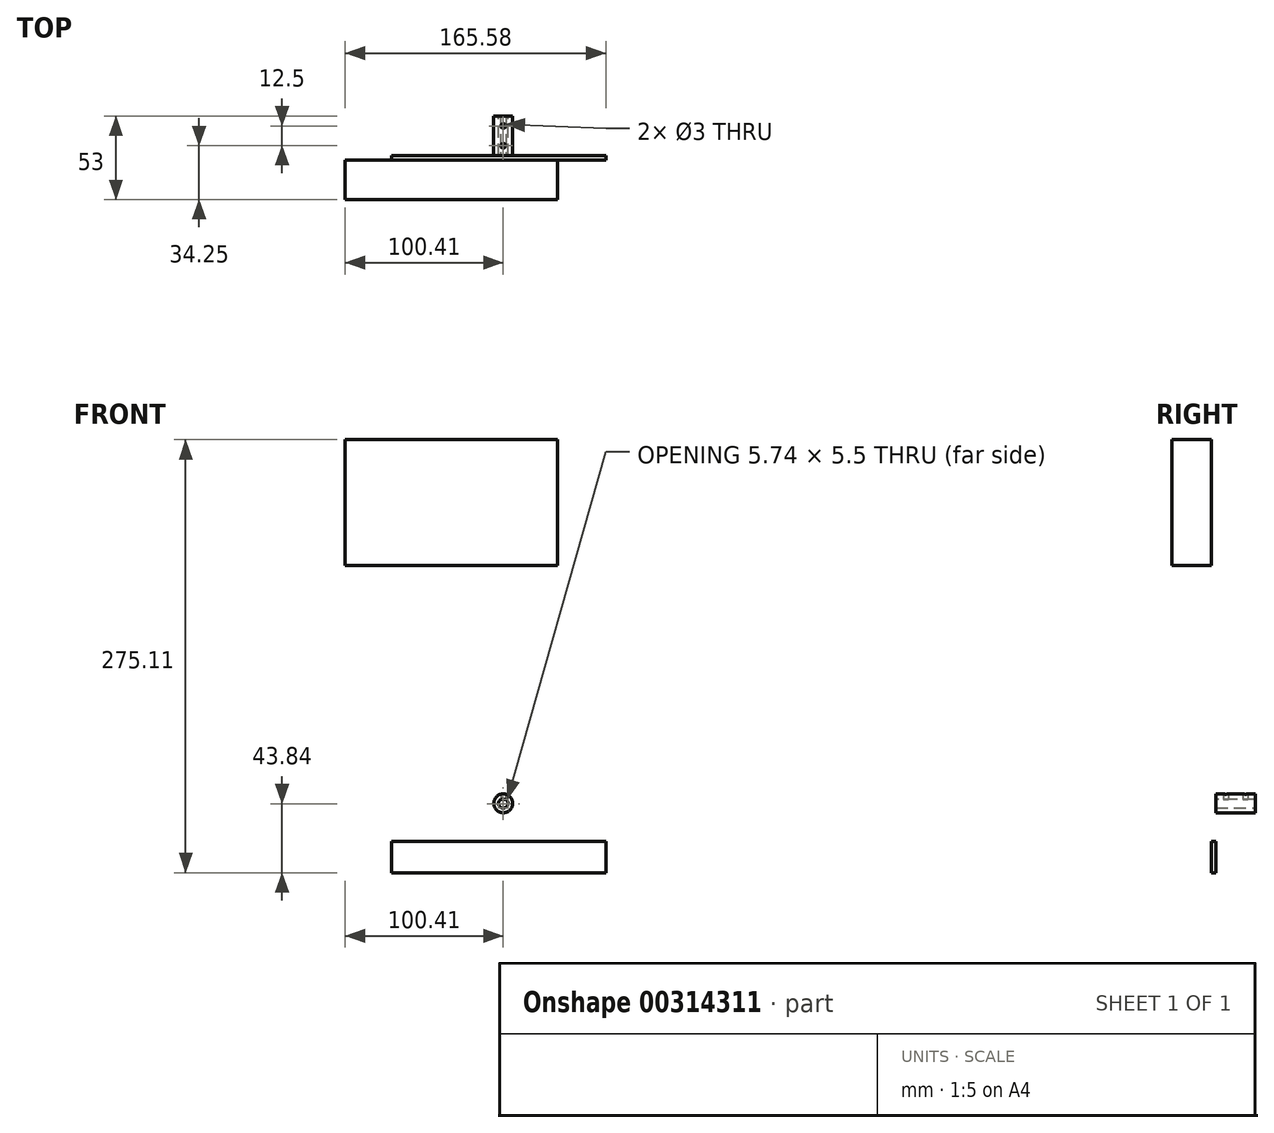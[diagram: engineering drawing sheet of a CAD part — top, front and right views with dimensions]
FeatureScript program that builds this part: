
annotation { "Feature Type Name" : "Feature", "Feature Type Description" : "" }
export const myFeature = defineFeature(function(context is Context, id is Id, definition is map)
    precondition{}
    {
        {
            var Q0;
            Q0=qCreatedBy(makeId("Front.planeOp"),FACE);
            var sketch = newSketch(context, id + "F0", { "sketchPlane" : qUnion([Q0])});
            skCircle(sketch, "E0", {"center": v(0, 0) * mm, "radius": 6 * mm});
            skSolve(sketch);
        }
        {
            var Q0;
            Q0=makeQuery(id+"F0.imprint","IMPRINT",FACE,{"disambiguationData":[TD([[makeQuery(id+"F0.imprint","IMPRINT",EDGE,{"derivedFrom":sQuery(id+"F0.wireOp",EDGE,"E0")}),1.0]])]});
            extrude(context, id + "F1", {"entities" : qUnion([Q0]), "depth" : 25 * mm});
        }
        {
            var Q0;
            Q0=qCreatedBy(makeId("Front.planeOp"),FACE);
            var sketch = newSketch(context, id + "F2", { "sketchPlane" : qUnion([Q0])});
            skCircle(sketch, "E1", {"center": v(0, 0) * mm, "radius": 3 * mm});
            skSolve(sketch);
        }
        {
            var Q0;
            Q0=makeQuery(id+"F2.imprint","IMPRINT",FACE,{"disambiguationData":[TD([[makeQuery(id+"F2.imprint","IMPRINT",EDGE,{"derivedFrom":sQuery(id+"F2.wireOp",EDGE,"E1")}),1.0]])]});
            var Q1;
            Q1=sQuery(id+"F2.wireOp",EDGE,"E1");
            var Q2;
            Q2=makeQuery(id+"F1.opExtrude","CAP_FACE",FACE,{"disambiguationData":[OSD([sQuery(id+"F0.wireOp",EDGE,"E0")])],"isStart":false});
            extrude(context, id + "F3", {"entities" : qUnion([Q0]), "operationType" : NewBodyOperationType.REMOVE, "surfaceEntities" : qUnion([Q1]), "endBound" : BoundingType.UP_TO_SURFACE, "endBoundEntityFace" : qUnion([Q2]), "depth" : 25 * mm});
        }
        {
            var Q0;
            Q0=makeQuery(id+"F1.opExtrude","CAP_FACE",FACE,{"disambiguationData":[OSD([sQuery(id+"F0.wireOp",EDGE,"E0")])],"isStart":false});
            var sketch = newSketch(context, id + "F4", { "sketchPlane" : qUnion([Q0])});
            skLineSegment(sketch, "E2", {"start": v(0, 2.5) * mm, "end": v(-1.66, 2.5) * mm});
            skLineSegment(sketch, "E3", {"start": v(-1.66, 2.5) * mm, "end": v(1.66, 2.5) * mm});
            skSolve(sketch);
        }
        {
            var Q0;
            Q0 = qSketchRegion(id + "F4", true);
            var Q1;
            {var subQ0=sQuery(id+"F4.wireOp",EDGE,"E3");var subQ3=makeQuery(id+"F4.imprint","IMPRINT",VERTEX,{"derivedFrom":subQ0});Q1=makeQuery(id+"F4.imprint","IMPRINT",FACE,{"disambiguationData":[TD([[makeQuery(id+"F4.imprint","IMPRINT",EDGE,{"disambiguationData":[TD([[subQ3,1.0]])],"derivedFrom":subQ0}),1.0]])]});}
            var Q2;
            Q2=makeQuery(id+"F1.opExtrude","CAP_FACE",FACE,{"disambiguationData":[OSD([sQuery(id+"F0.wireOp",EDGE,"E0")])],"isStart":true});
            extrude(context, id + "F5", {"entities" : qUnion([Q0, Q1]), "operationType" : NewBodyOperationType.ADD, "endBound" : BoundingType.UP_TO_SURFACE, "oppositeDirection" : true, "endBoundEntityFace" : qUnion([Q2]), "depth" : 25 * mm});
        }
        {
            var Q0;
            Q0=makeQuery(id+"F5.opExtrude","SWEPT_FACE",FACE,{"disambiguationData":[OSD([sQuery(id+"F4.wireOp",EDGE,"E3")])]});
            var sketch = newSketch(context, id + "F6", { "sketchPlane" : qUnion([Q0])});
            skLineSegment(sketch, "E4", {"start": v(-1.66, 12.5) * mm, "end": v(1.66, 12.5) * mm, "construction": true});
            skLineSegment(sketch, "E5", {"start": v(0, 12.5) * mm, "end": v(0, 25) * mm, "construction": true});
            skLineSegment(sketch, "E6", {"start": v(0, 12.5) * mm, "end": v(0, 0) * mm, "construction": true});
            skCircle(sketch, "E7", {"center": v(0, 18.75) * mm, "radius": 1.5 * mm});
            skCircle(sketch, "E8", {"center": v(0, 6.25) * mm, "radius": 1.5 * mm});
            skSolve(sketch);
        }
        {
            var Q0;
            Q0=makeQuery(id+"F6.imprint","IMPRINT",FACE,{"disambiguationData":[TD([[makeQuery(id+"F6.imprint","IMPRINT",EDGE,{"derivedFrom":sQuery(id+"F6.wireOp",EDGE,"E7")}),1.0]])]});
            var Q1;
            Q1=makeQuery(id+"F6.imprint","IMPRINT",FACE,{"disambiguationData":[TD([[makeQuery(id+"F6.imprint","IMPRINT",EDGE,{"derivedFrom":sQuery(id+"F6.wireOp",EDGE,"E8")}),1.0]])]});
            extrude(context, id + "F7", {"entities" : qUnion([Q0, Q1]), "operationType" : NewBodyOperationType.REMOVE, "endBound" : BoundingType.UP_TO_NEXT, "oppositeDirection" : true, "depth" : 25 * mm});
        }
        {
            var Q0;
            {var subQ0=sQuery(id+"F0.wireOp",EDGE,"E0");Q0=makeQuery(id+"F5.boolean.opBoolean","MERGE",FACE,{"derivedFrom":[makeQuery(id+"F1.opExtrude","CAP_FACE",FACE,{"disambiguationData":[OSD([subQ0])],"isStart":false}),makeQuery(id+"F5.opExtrude","CAP_FACE",FACE,{"disambiguationData":[OSD([subQ0,sQuery(id+"F2.wireOp",EDGE,"E1"),sQuery(id+"F4.wireOp",EDGE,"E3")])],"isStart":true})]});}
            var sketch = newSketch(context, id + "F8", { "sketchPlane" : qUnion([Q0])});
            skLineSegment(sketch, "E9.bottom", {"start": v(-70.83, -24.09) * mm, "end": v(65.17, -24.09) * mm});
            skLineSegment(sketch, "E9.top", {"start": v(-70.83, -44.09) * mm, "end": v(65.17, -44.09) * mm});
            skLineSegment(sketch, "E9.left", {"start": v(-70.83, -24.09) * mm, "end": v(-70.83, -44.09) * mm});
            skLineSegment(sketch, "E9.right", {"start": v(65.17, -24.09) * mm, "end": v(65.17, -44.09) * mm});
            skSolve(sketch);
        }
        {
            var Q0;
            Q0 = qSketchRegion(id + "F8", true);
            extrude(context, id + "F9", {"entities" : qUnion([Q0]), "depth" : 3 * mm});
        }
        {
            var Q0;
            {var subQ0=sQuery(id+"F0.wireOp",EDGE,"E0");Q0=makeQuery(id+"F5.boolean.opBoolean","MERGE",FACE,{"derivedFrom":[makeQuery(id+"F1.opExtrude","CAP_FACE",FACE,{"disambiguationData":[OSD([subQ0])],"isStart":false}),makeQuery(id+"F5.opExtrude","CAP_FACE",FACE,{"disambiguationData":[OSD([subQ0,sQuery(id+"F2.wireOp",EDGE,"E1"),sQuery(id+"F4.wireOp",EDGE,"E3")])],"isStart":true})]});}
            var sketch = newSketch(context, id + "F10", { "sketchPlane" : qUnion([Q0])});
            skSolve(sketch);
        }
        {
            var Q0;
            Q0=makeQuery(id+"F9.opExtrude","CAP_FACE",FACE,{"disambiguationData":[OSD([sQuery(id+"F8.wireOp",EDGE,"E9.bottom"),sQuery(id+"F8.wireOp",EDGE,"E9.top"),sQuery(id+"F8.wireOp",EDGE,"E9.left"),sQuery(id+"F8.wireOp",EDGE,"E9.right")])],"isStart":false});
            var sketch = newSketch(context, id + "F11", { "sketchPlane" : qUnion([Q0])});
            skLineSegment(sketch, "E10.bottom", {"start": v(-100.41, 231.02) * mm, "end": v(34.59, 231.02) * mm});
            skLineSegment(sketch, "E10.top", {"start": v(-100.41, 151.02) * mm, "end": v(34.59, 151.02) * mm});
            skLineSegment(sketch, "E10.left", {"start": v(-100.41, 231.02) * mm, "end": v(-100.41, 151.02) * mm});
            skLineSegment(sketch, "E10.right", {"start": v(34.59, 231.02) * mm, "end": v(34.59, 151.02) * mm});
            skSolve(sketch);
        }
        {
            var Q0;
            Q0=makeQuery(id+"F11.imprint","IMPRINT",FACE,{"disambiguationData":[TD([[makeQuery(id+"F11.imprint","IMPRINT",EDGE,{"derivedFrom":sQuery(id+"F11.wireOp",EDGE,"E10.bottom")}),-1.0]])]});
            extrude(context, id + "F12", {"entities" : qUnion([Q0]), "depth" : 25 * mm});
        }
    });
